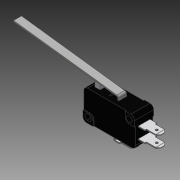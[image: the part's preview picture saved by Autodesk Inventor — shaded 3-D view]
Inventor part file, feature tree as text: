
AUTODESK INVENTOR PART (.ipt)
format: ipt  version: 2014 SP1 (Build 180222100, 222)  size: 226,304 bytes
history: native  units: in
note: dims shown in document units (in); Inventor stores cm internally (conversion verified against a paired STEP export)
features: other x4, imported_body x3, extrude x1, sketch x1
ambient origin geometry x8: Origin, YZ Plane, XZ Plane, XY Plane, X Axis, Y Axis, Z Axis, Center Point
bodies: Body1 (feature_tree), Body2 (feature_tree), Body3 (feature_tree)
feature tree (9):
  parser-record x1  (decoder bookkeeping rows leaked as tree rows — omitted from the tree; the rows remain in map.json)
  other  "7779K6301"
  extrude  "Extrusion1"  [1 undecoded]
  other  "NONE_1"
  other  "NONE_2"
  imported_body  "Base1"
  imported_body  "Base2"
  imported_body  "Base3"
  sketch  "Sketch1"  dims[d0=1.1811in d1=0.0in]
note: 1 required parameter value undecoded (feature->parameter linkage not recoverable at this tier; creation-order binding heuristic only, values carry confidence <= 0.55)
